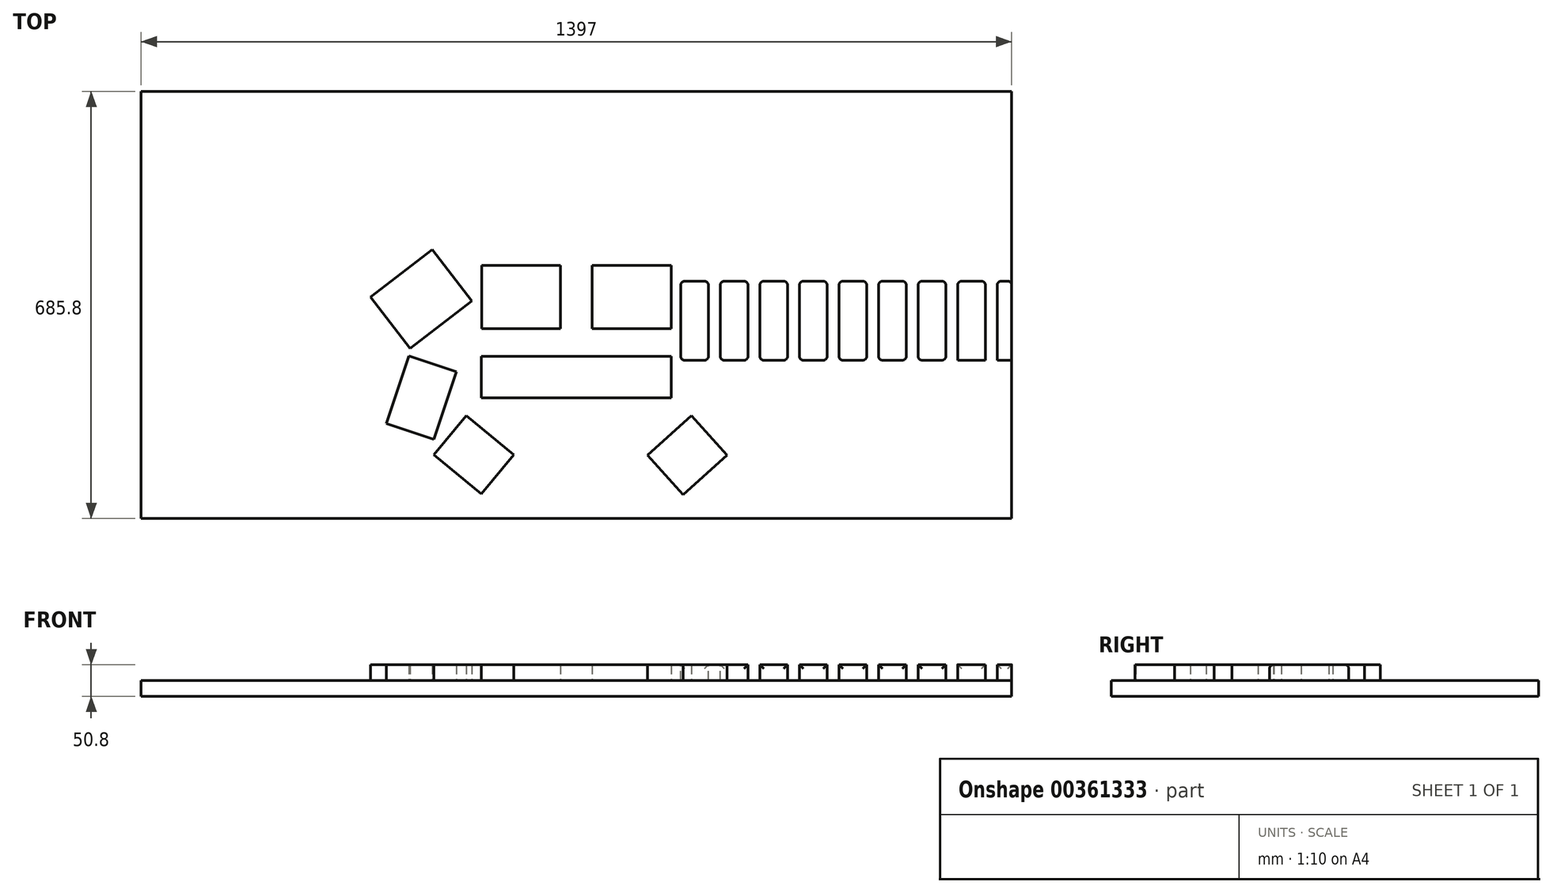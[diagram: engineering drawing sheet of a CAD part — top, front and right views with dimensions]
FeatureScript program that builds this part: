
annotation { "Feature Type Name" : "Feature", "Feature Type Description" : "" }
export const myFeature = defineFeature(function(context is Context, id is Id, definition is map)
    precondition{}
    {
        {
            var Q0;
            Q0=qCreatedBy(makeId("Top.planeOp"),FACE);
            var sketch = newSketch(context, id + "F0", { "sketchPlane" : qUnion([Q0])});
            skLineSegment(sketch, "E0.bottom", {"start": v(698.5, 313.84) * mm, "end": v(-698.5, 313.84) * mm});
            skLineSegment(sketch, "E0.top", {"start": v(698.5, -371.96) * mm, "end": v(-698.5, -371.96) * mm});
            skLineSegment(sketch, "E0.left", {"start": v(698.5, 313.84) * mm, "end": v(698.5, -371.96) * mm});
            skLineSegment(sketch, "E0.right", {"start": v(-698.5, 313.84) * mm, "end": v(-698.5, -371.96) * mm});
            skPoint(sketch, "E0.middle", {"position": v(0, -29.06) * mm});
            skSolve(sketch);
        }
        {
            var Q0;
            Q0=qSketchRegion(id+"F0",true);
            extrude(context, id + "F1", {"entities" : qUnion([Q0]), "depth" : 25.4 * mm});
        }
        {
            var Q0;
            Q0=makeQuery(id+"F1.opExtrude","CAP_FACE",FACE,{"disambiguationData":[OSD([sQuery(id+"F0.wireOp",EDGE,"E0.bottom"),sQuery(id+"F0.wireOp",EDGE,"E0.top"),sQuery(id+"F0.wireOp",EDGE,"E0.left"),sQuery(id+"F0.wireOp",EDGE,"E0.right")])],"isStart":false});
            var sketch = newSketch(context, id + "F2", { "sketchPlane" : qUnion([Q0])});
            skLineSegment(sketch, "E1.bottom", {"start": v(152.4, -111.6) * mm, "end": v(-152.4, -111.6) * mm});
            skLineSegment(sketch, "E1.top", {"start": v(152.4, -178.28) * mm, "end": v(-152.4, -178.28) * mm});
            skLineSegment(sketch, "E1.left", {"start": v(152.4, -111.6) * mm, "end": v(152.4, -178.28) * mm});
            skLineSegment(sketch, "E1.right", {"start": v(-152.4, -111.6) * mm, "end": v(-152.4, -178.28) * mm});
            skPoint(sketch, "E1.middle", {"position": v(0, -144.94) * mm});
            skLineSegment(sketch, "E2.bottom", {"start": v(-25.4, -67.16) * mm, "end": v(-151.9, -67.16) * mm});
            skLineSegment(sketch, "E2.top", {"start": v(-25.4, 34.44) * mm, "end": v(-151.9, 34.44) * mm});
            skLineSegment(sketch, "E2.left", {"start": v(-25.4, -67.16) * mm, "end": v(-25.4, 34.44) * mm});
            skLineSegment(sketch, "E2.right", {"start": v(-151.9, -67.16) * mm, "end": v(-151.9, 34.44) * mm});
            skPoint(sketch, "E2.middle", {"position": v(-88.65, -16.36) * mm});
            skPoint(sketch, "E3", {"position": v(-88.65, -67.16) * mm});
            skLineSegment(sketch, "E4.bottom", {"start": v(152.4, -67.25) * mm, "end": v(25.4, -67.25) * mm});
            skLineSegment(sketch, "E4.top", {"start": v(152.4, 34.44) * mm, "end": v(25.4, 34.44) * mm});
            skLineSegment(sketch, "E4.left", {"start": v(152.4, -67.25) * mm, "end": v(152.4, 34.44) * mm});
            skLineSegment(sketch, "E4.right", {"start": v(25.4, -67.25) * mm, "end": v(25.4, 34.44) * mm});
            skPoint(sketch, "E4.middle", {"position": v(88.9, -16.4) * mm});
            skPoint(sketch, "E5", {"position": v(88.9, -67.25) * mm});
            skLineSegment(sketch, "E6.bottom", {"start": v(-100.46, -269.65) * mm, "end": v(-152.4, -332.56) * mm});
            skLineSegment(sketch, "E6.top", {"start": v(-176.66, -206.74) * mm, "end": v(-228.6, -269.65) * mm});
            skLineSegment(sketch, "E6.left", {"start": v(-100.46, -269.65) * mm, "end": v(-176.66, -206.74) * mm});
            skLineSegment(sketch, "E6.right", {"start": v(-152.4, -332.56) * mm, "end": v(-228.6, -269.65) * mm});
            skPoint(sketch, "E6.middle", {"position": v(-164.53, -269.65) * mm});
            skLineSegment(sketch, "E7.bottom", {"start": v(-192.38, -136.29) * mm, "end": v(-228.6, -244.96) * mm});
            skLineSegment(sketch, "E7.top", {"start": v(-268.58, -110.89) * mm, "end": v(-304.8, -219.56) * mm});
            skLineSegment(sketch, "E7.left", {"start": v(-192.38, -136.29) * mm, "end": v(-268.58, -110.89) * mm});
            skLineSegment(sketch, "E7.right", {"start": v(-228.6, -244.96) * mm, "end": v(-304.8, -219.56) * mm});
            skPoint(sketch, "E7.middle", {"position": v(-248.59, -177.92) * mm});
            skLineSegment(sketch, "E8.bottom", {"start": v(-167.77, -22.8) * mm, "end": v(-266.7, -98.9) * mm});
            skLineSegment(sketch, "E8.top", {"start": v(-231.27, 59.74) * mm, "end": v(-330.2, -16.36) * mm});
            skLineSegment(sketch, "E8.left", {"start": v(-167.77, -22.8) * mm, "end": v(-231.27, 59.74) * mm});
            skLineSegment(sketch, "E8.right", {"start": v(-266.7, -98.9) * mm, "end": v(-330.2, -16.36) * mm});
            skPoint(sketch, "E8.middle", {"position": v(-248.99, -19.58) * mm});
            skLineSegment(sketch, "E9.bottom", {"start": v(114.3, -270.36) * mm, "end": v(184.86, -206.86) * mm});
            skLineSegment(sketch, "E9.top", {"start": v(171.45, -333.86) * mm, "end": v(242, -270.36) * mm});
            skLineSegment(sketch, "E9.left", {"start": v(114.3, -270.36) * mm, "end": v(171.45, -333.86) * mm});
            skLineSegment(sketch, "E9.right", {"start": v(184.86, -206.86) * mm, "end": v(242, -270.36) * mm});
            skPoint(sketch, "E9.middle", {"position": v(178.15, -270.36) * mm});
            skPoint(sketch, "E10", {"position": v(206.73, -302.1) * mm});
            skSolve(sketch);
        }
        {
            var Q0;
            Q0=qSketchRegion(id+"F2",true);
            extrude(context, id + "F3", {"entities" : qUnion([Q0]), "depth" : 25.4 * mm});
        }
        {
            var Q0;
            Q0=makeQuery(id+"F1.opExtrude","CAP_FACE",FACE,{"disambiguationData":[OSD([sQuery(id+"F0.wireOp",EDGE,"E0.bottom"),sQuery(id+"F0.wireOp",EDGE,"E0.top"),sQuery(id+"F0.wireOp",EDGE,"E0.left"),sQuery(id+"F0.wireOp",EDGE,"E0.right")])],"isStart":false});
            var sketch = newSketch(context, id + "F4", { "sketchPlane" : qUnion([Q0])});
            skLineSegment(sketch, "E11.bottom", {"start": v(802.42, -117.9) * mm, "end": v(167.42, -118.01) * mm});
            skLineSegment(sketch, "E11.top", {"start": v(802.4, 9.1) * mm, "end": v(167.4, 8.99) * mm});
            skLineSegment(sketch, "E11.left", {"start": v(802.42, -117.9) * mm, "end": v(802.4, 9.1) * mm});
            skLineSegment(sketch, "E11.right", {"start": v(167.42, -118.01) * mm, "end": v(167.4, 8.99) * mm});
            skSolve(sketch);
        }
        {
            var Q0;
            Q0 = qSketchRegion(id + "F4", true);
            extrude(context, id + "F5", {"entities" : qUnion([Q0]), "operationType" : NewBodyOperationType.ADD, "depth" : 25.4 * mm});
        }
        {
            var Q0;
            Q0=makeQuery(id+"F5.opExtrude","SWEPT_FACE",FACE,{"disambiguationData":[OSD([sQuery(id+"F4.wireOp",EDGE,"E11.bottom")])]});
            var sketch = newSketch(context, id + "F6", { "sketchPlane" : qUnion([Q0])});
            skLineSegment(sketch, "E12.bottom", {"start": v(698.48, 25.4) * mm, "end": v(802.4, 25.4) * mm});
            skLineSegment(sketch, "E12.top", {"start": v(698.48, 50.8) * mm, "end": v(802.4, 50.8) * mm});
            skLineSegment(sketch, "E12.left", {"start": v(698.48, 25.4) * mm, "end": v(698.48, 50.8) * mm});
            skLineSegment(sketch, "E12.right", {"start": v(802.4, 25.4) * mm, "end": v(802.4, 50.8) * mm});
            skPoint(sketch, "E13", {"position": v(167.4, 50.8) * mm});
            skPoint(sketch, "E14", {"position": v(211.86, 50.8) * mm});
            skPoint(sketch, "E15", {"position": v(230.9, 50.8) * mm});
            skPoint(sketch, "E16", {"position": v(275.36, 50.8) * mm});
            skPoint(sketch, "E17", {"position": v(294.4, 50.8) * mm});
            skPoint(sketch, "E18", {"position": v(338.86, 50.8) * mm});
            skPoint(sketch, "E19", {"position": v(357.9, 50.8) * mm});
            skPoint(sketch, "E20", {"position": v(402.36, 50.8) * mm});
            skPoint(sketch, "E21", {"position": v(421.4, 50.8) * mm});
            skPoint(sketch, "E22", {"position": v(465.86, 50.8) * mm});
            skPoint(sketch, "E23", {"position": v(484.9, 50.8) * mm});
            skPoint(sketch, "E24", {"position": v(529.36, 50.8) * mm});
            skPoint(sketch, "E25", {"position": v(548.4, 50.8) * mm});
            skPoint(sketch, "E26", {"position": v(592.86, 50.8) * mm});
            skPoint(sketch, "E27", {"position": v(611.9, 50.8) * mm});
            skPoint(sketch, "E28", {"position": v(656.36, 50.8) * mm});
            skPoint(sketch, "E29", {"position": v(675.4, 50.8) * mm});
            skLineSegment(sketch, "E30.bottom", {"start": v(675.4, 50.8) * mm, "end": v(656.36, 50.8) * mm});
            skLineSegment(sketch, "E30.top", {"start": v(675.4, 25.4) * mm, "end": v(656.36, 25.4) * mm});
            skLineSegment(sketch, "E30.left", {"start": v(675.4, 50.8) * mm, "end": v(675.4, 25.4) * mm});
            skLineSegment(sketch, "E30.right", {"start": v(656.36, 50.8) * mm, "end": v(656.36, 25.4) * mm});
            skLineSegment(sketch, "E31.bottom", {"start": v(611.9, 25.4) * mm, "end": v(592.86, 25.4) * mm});
            skLineSegment(sketch, "E31.top", {"start": v(611.9, 50.8) * mm, "end": v(592.86, 50.8) * mm});
            skLineSegment(sketch, "E31.left", {"start": v(611.9, 25.4) * mm, "end": v(611.9, 50.8) * mm});
            skLineSegment(sketch, "E31.right", {"start": v(592.86, 25.4) * mm, "end": v(592.86, 50.8) * mm});
            skLineSegment(sketch, "E32.bottom", {"start": v(548.4, 25.4) * mm, "end": v(529.36, 25.4) * mm});
            skLineSegment(sketch, "E32.top", {"start": v(548.4, 50.8) * mm, "end": v(529.36, 50.8) * mm});
            skLineSegment(sketch, "E32.left", {"start": v(548.4, 25.4) * mm, "end": v(548.4, 50.8) * mm});
            skLineSegment(sketch, "E32.right", {"start": v(529.36, 25.4) * mm, "end": v(529.36, 50.8) * mm});
            skLineSegment(sketch, "E33.bottom", {"start": v(484.9, 25.4) * mm, "end": v(465.86, 25.4) * mm});
            skLineSegment(sketch, "E33.top", {"start": v(484.9, 50.8) * mm, "end": v(465.86, 50.8) * mm});
            skLineSegment(sketch, "E33.left", {"start": v(484.9, 25.4) * mm, "end": v(484.9, 50.8) * mm});
            skLineSegment(sketch, "E33.right", {"start": v(465.86, 25.4) * mm, "end": v(465.86, 50.8) * mm});
            skLineSegment(sketch, "E34.bottom", {"start": v(421.4, 25.4) * mm, "end": v(402.36, 25.4) * mm});
            skLineSegment(sketch, "E34.top", {"start": v(421.4, 50.8) * mm, "end": v(402.36, 50.8) * mm});
            skLineSegment(sketch, "E34.left", {"start": v(421.4, 25.4) * mm, "end": v(421.4, 50.8) * mm});
            skLineSegment(sketch, "E34.right", {"start": v(402.36, 25.4) * mm, "end": v(402.36, 50.8) * mm});
            skLineSegment(sketch, "E35.bottom", {"start": v(357.9, 25.4) * mm, "end": v(338.86, 25.4) * mm});
            skLineSegment(sketch, "E35.top", {"start": v(357.9, 50.8) * mm, "end": v(338.86, 50.8) * mm});
            skLineSegment(sketch, "E35.left", {"start": v(357.9, 25.4) * mm, "end": v(357.9, 50.8) * mm});
            skLineSegment(sketch, "E35.right", {"start": v(338.86, 25.4) * mm, "end": v(338.86, 50.8) * mm});
            skLineSegment(sketch, "E36.bottom", {"start": v(294.4, 25.4) * mm, "end": v(275.36, 25.4) * mm});
            skLineSegment(sketch, "E36.top", {"start": v(294.4, 50.8) * mm, "end": v(275.36, 50.8) * mm});
            skLineSegment(sketch, "E36.left", {"start": v(294.4, 25.4) * mm, "end": v(294.4, 50.8) * mm});
            skLineSegment(sketch, "E36.right", {"start": v(275.36, 25.4) * mm, "end": v(275.36, 50.8) * mm});
            skLineSegment(sketch, "E37.bottom", {"start": v(230.9, 25.4) * mm, "end": v(211.86, 25.4) * mm});
            skLineSegment(sketch, "E37.top", {"start": v(230.9, 50.8) * mm, "end": v(211.86, 50.8) * mm});
            skLineSegment(sketch, "E37.left", {"start": v(230.9, 25.4) * mm, "end": v(230.9, 50.8) * mm});
            skLineSegment(sketch, "E37.right", {"start": v(211.86, 25.4) * mm, "end": v(211.86, 50.8) * mm});
            skSolve(sketch);
        }
        {
            var Q0;
            Q0 = qSketchRegion(id + "F6", true);
            extrude(context, id + "F7", {"entities" : qUnion([Q0]), "operationType" : NewBodyOperationType.REMOVE, "oppositeDirection" : true, "depth" : 203.2 * mm});
        }
        {
            var Q0;
            {var subQ0=sQuery(id+"F4.wireOp",EDGE,"E11.bottom");var subQ1=sQuery(id+"F4.wireOp",EDGE,"E11.right");Q0=makeQuery(id+"F7.boolean.opBoolean","SPLIT",EDGE,{"disambiguationData":[TD([makeQuery(id+"F5.opExtrude","SWEPT_FACE",FACE,{"disambiguationData":[OSD([subQ1])]})])],"derivedFrom":makeQuery(id+"F5.opExtrude","CAP_EDGE",EDGE,{"disambiguationData":[OSD([subQ0])],"isStart":false})});}
            var Q1;
            {var subQ0=sQuery(id+"F4.wireOp",EDGE,"E11.bottom");Q1=makeQuery(id+"F7.boolean.opBoolean","SPLIT",EDGE,{"disambiguationData":[TD([makeQuery(id+"F7.opExtrude","SWEPT_FACE",FACE,{"disambiguationData":[OSD([sQuery(id+"F6.wireOp",EDGE,"E36.right")])]})])],"derivedFrom":makeQuery(id+"F5.opExtrude","CAP_EDGE",EDGE,{"disambiguationData":[OSD([subQ0])],"isStart":false})});}
            var Q2;
            {var subQ0=sQuery(id+"F4.wireOp",EDGE,"E11.bottom");Q2=makeQuery(id+"F7.boolean.opBoolean","SPLIT",EDGE,{"disambiguationData":[TD([makeQuery(id+"F7.opExtrude","SWEPT_FACE",FACE,{"disambiguationData":[OSD([sQuery(id+"F6.wireOp",EDGE,"E35.right")])]})])],"derivedFrom":makeQuery(id+"F5.opExtrude","CAP_EDGE",EDGE,{"disambiguationData":[OSD([subQ0])],"isStart":false})});}
            var Q3;
            {var subQ0=sQuery(id+"F4.wireOp",EDGE,"E11.bottom");Q3=makeQuery(id+"F7.boolean.opBoolean","SPLIT",EDGE,{"disambiguationData":[TD([makeQuery(id+"F7.opExtrude","SWEPT_FACE",FACE,{"disambiguationData":[OSD([sQuery(id+"F6.wireOp",EDGE,"E34.right")])]})])],"derivedFrom":makeQuery(id+"F5.opExtrude","CAP_EDGE",EDGE,{"disambiguationData":[OSD([subQ0])],"isStart":false})});}
            var Q4;
            {var subQ0=sQuery(id+"F4.wireOp",EDGE,"E11.bottom");Q4=makeQuery(id+"F7.boolean.opBoolean","SPLIT",EDGE,{"disambiguationData":[TD([makeQuery(id+"F7.opExtrude","SWEPT_FACE",FACE,{"disambiguationData":[OSD([sQuery(id+"F6.wireOp",EDGE,"E33.right")])]})])],"derivedFrom":makeQuery(id+"F5.opExtrude","CAP_EDGE",EDGE,{"disambiguationData":[OSD([subQ0])],"isStart":false})});}
            var Q5;
            {var subQ0=sQuery(id+"F4.wireOp",EDGE,"E11.bottom");Q5=makeQuery(id+"F7.boolean.opBoolean","SPLIT",EDGE,{"disambiguationData":[TD([makeQuery(id+"F7.opExtrude","SWEPT_FACE",FACE,{"disambiguationData":[OSD([sQuery(id+"F6.wireOp",EDGE,"E32.right")])]})])],"derivedFrom":makeQuery(id+"F5.opExtrude","CAP_EDGE",EDGE,{"disambiguationData":[OSD([subQ0])],"isStart":false})});}
            var Q6;
            {var subQ0=sQuery(id+"F4.wireOp",EDGE,"E11.bottom");Q6=makeQuery(id+"F7.boolean.opBoolean","SPLIT",EDGE,{"disambiguationData":[TD([makeQuery(id+"F7.opExtrude","SWEPT_FACE",FACE,{"disambiguationData":[OSD([sQuery(id+"F6.wireOp",EDGE,"E31.right")])]})])],"derivedFrom":makeQuery(id+"F5.opExtrude","CAP_EDGE",EDGE,{"disambiguationData":[OSD([subQ0])],"isStart":false})});}
            var Q7;
            {var subQ0=sQuery(id+"F4.wireOp",EDGE,"E11.bottom");Q7=makeQuery(id+"F7.boolean.opBoolean","SPLIT",EDGE,{"disambiguationData":[TD([makeQuery(id+"F7.opExtrude","SWEPT_FACE",FACE,{"disambiguationData":[OSD([sQuery(id+"F6.wireOp",EDGE,"E30.right")])]})])],"derivedFrom":makeQuery(id+"F5.opExtrude","CAP_EDGE",EDGE,{"disambiguationData":[OSD([subQ0])],"isStart":false})});}
            var Q8;
            {var subQ0=sQuery(id+"F4.wireOp",EDGE,"E11.top");Q8=makeQuery(id+"F7.boolean.opBoolean","SPLIT",EDGE,{"disambiguationData":[TD([makeQuery(id+"F7.opExtrude","SWEPT_FACE",FACE,{"disambiguationData":[OSD([sQuery(id+"F6.wireOp",EDGE,"E30.right")])]})])],"derivedFrom":makeQuery(id+"F5.opExtrude","CAP_EDGE",EDGE,{"disambiguationData":[OSD([subQ0])],"isStart":false})});}
            var Q9;
            {var subQ0=sQuery(id+"F4.wireOp",EDGE,"E11.top");Q9=makeQuery(id+"F7.boolean.opBoolean","SPLIT",EDGE,{"disambiguationData":[TD([makeQuery(id+"F7.opExtrude","SWEPT_FACE",FACE,{"disambiguationData":[OSD([sQuery(id+"F6.wireOp",EDGE,"E12.left")])]})])],"derivedFrom":makeQuery(id+"F5.opExtrude","CAP_EDGE",EDGE,{"disambiguationData":[OSD([subQ0])],"isStart":false})});}
            var Q10;
            {var subQ0=sQuery(id+"F4.wireOp",EDGE,"E11.bottom");Q10=makeQuery(id+"F7.boolean.opBoolean","SPLIT",EDGE,{"disambiguationData":[TD([makeQuery(id+"F7.opExtrude","SWEPT_FACE",FACE,{"disambiguationData":[OSD([sQuery(id+"F6.wireOp",EDGE,"E12.left")])]})])],"derivedFrom":makeQuery(id+"F5.opExtrude","CAP_EDGE",EDGE,{"disambiguationData":[OSD([subQ0])],"isStart":false})});}
            var Q11;
            {var subQ0=sQuery(id+"F4.wireOp",EDGE,"E11.top");Q11=makeQuery(id+"F7.boolean.opBoolean","SPLIT",EDGE,{"disambiguationData":[TD([makeQuery(id+"F7.opExtrude","SWEPT_FACE",FACE,{"disambiguationData":[OSD([sQuery(id+"F6.wireOp",EDGE,"E31.right")])]})])],"derivedFrom":makeQuery(id+"F5.opExtrude","CAP_EDGE",EDGE,{"disambiguationData":[OSD([subQ0])],"isStart":false})});}
            var Q12;
            {var subQ0=sQuery(id+"F4.wireOp",EDGE,"E11.top");Q12=makeQuery(id+"F7.boolean.opBoolean","SPLIT",EDGE,{"disambiguationData":[TD([makeQuery(id+"F7.opExtrude","SWEPT_FACE",FACE,{"disambiguationData":[OSD([sQuery(id+"F6.wireOp",EDGE,"E32.right")])]})])],"derivedFrom":makeQuery(id+"F5.opExtrude","CAP_EDGE",EDGE,{"disambiguationData":[OSD([subQ0])],"isStart":false})});}
            var Q13;
            {var subQ0=sQuery(id+"F4.wireOp",EDGE,"E11.top");Q13=makeQuery(id+"F7.boolean.opBoolean","SPLIT",EDGE,{"disambiguationData":[TD([makeQuery(id+"F7.opExtrude","SWEPT_FACE",FACE,{"disambiguationData":[OSD([sQuery(id+"F6.wireOp",EDGE,"E33.right")])]})])],"derivedFrom":makeQuery(id+"F5.opExtrude","CAP_EDGE",EDGE,{"disambiguationData":[OSD([subQ0])],"isStart":false})});}
            var Q14;
            {var subQ0=sQuery(id+"F4.wireOp",EDGE,"E11.right");var subQ1=sQuery(id+"F4.wireOp",EDGE,"E11.top");Q14=makeQuery(id+"F7.boolean.opBoolean","SPLIT",EDGE,{"disambiguationData":[TD([makeQuery(id+"F5.opExtrude","SWEPT_FACE",FACE,{"disambiguationData":[OSD([subQ0])]})])],"derivedFrom":makeQuery(id+"F5.opExtrude","CAP_EDGE",EDGE,{"disambiguationData":[OSD([subQ1])],"isStart":false})});}
            var Q15;
            {var subQ0=sQuery(id+"F4.wireOp",EDGE,"E11.top");Q15=makeQuery(id+"F7.boolean.opBoolean","SPLIT",EDGE,{"disambiguationData":[TD([makeQuery(id+"F7.opExtrude","SWEPT_FACE",FACE,{"disambiguationData":[OSD([sQuery(id+"F6.wireOp",EDGE,"E36.right")])]})])],"derivedFrom":makeQuery(id+"F5.opExtrude","CAP_EDGE",EDGE,{"disambiguationData":[OSD([subQ0])],"isStart":false})});}
            var Q16;
            {var subQ0=sQuery(id+"F4.wireOp",EDGE,"E11.top");Q16=makeQuery(id+"F7.boolean.opBoolean","SPLIT",EDGE,{"disambiguationData":[TD([makeQuery(id+"F7.opExtrude","SWEPT_FACE",FACE,{"disambiguationData":[OSD([sQuery(id+"F6.wireOp",EDGE,"E35.right")])]})])],"derivedFrom":makeQuery(id+"F5.opExtrude","CAP_EDGE",EDGE,{"disambiguationData":[OSD([subQ0])],"isStart":false})});}
            var Q17;
            {var subQ0=sQuery(id+"F4.wireOp",EDGE,"E11.top");Q17=makeQuery(id+"F7.boolean.opBoolean","SPLIT",EDGE,{"disambiguationData":[TD([makeQuery(id+"F7.opExtrude","SWEPT_FACE",FACE,{"disambiguationData":[OSD([sQuery(id+"F6.wireOp",EDGE,"E34.right")])]})])],"derivedFrom":makeQuery(id+"F5.opExtrude","CAP_EDGE",EDGE,{"disambiguationData":[OSD([subQ0])],"isStart":false})});}
            var Q18;
            Q18=makeQuery(id+"F5.opExtrude","SWEPT_EDGE",EDGE,{"disambiguationData":[OSD([sQuery(id+"F4.wireOp",EDGE,"E11.bottom"),sQuery(id+"F4.wireOp",EDGE,"E11.right")])]});
            var Q19;
            Q19=makeQuery(id+"F7.boolean.opBoolean","COPY",EDGE,{"derivedFrom":makeQuery(id+"F7.opExtrude","CAP_EDGE",EDGE,{"disambiguationData":[OSD([sQuery(id+"F6.wireOp",EDGE,"E37.right")])],"isStart":true})});
            var Q20;
            Q20=makeQuery(id+"F7.boolean.opBoolean","COPY",EDGE,{"derivedFrom":makeQuery(id+"F7.opExtrude","CAP_EDGE",EDGE,{"disambiguationData":[OSD([sQuery(id+"F6.wireOp",EDGE,"E37.left")])],"isStart":true})});
            var Q21;
            Q21=makeQuery(id+"F7.boolean.opBoolean","COPY",EDGE,{"derivedFrom":makeQuery(id+"F7.opExtrude","CAP_EDGE",EDGE,{"disambiguationData":[OSD([sQuery(id+"F6.wireOp",EDGE,"E36.right")])],"isStart":true})});
            var Q22;
            Q22=makeQuery(id+"F7.boolean.opBoolean","COPY",EDGE,{"derivedFrom":makeQuery(id+"F7.opExtrude","CAP_EDGE",EDGE,{"disambiguationData":[OSD([sQuery(id+"F6.wireOp",EDGE,"E36.left")])],"isStart":true})});
            var Q23;
            Q23=makeQuery(id+"F7.boolean.opBoolean","COPY",EDGE,{"derivedFrom":makeQuery(id+"F7.opExtrude","CAP_EDGE",EDGE,{"disambiguationData":[OSD([sQuery(id+"F6.wireOp",EDGE,"E35.right")])],"isStart":true})});
            var Q24;
            Q24=makeQuery(id+"F7.boolean.opBoolean","COPY",EDGE,{"derivedFrom":makeQuery(id+"F7.opExtrude","CAP_EDGE",EDGE,{"disambiguationData":[OSD([sQuery(id+"F6.wireOp",EDGE,"E35.left")])],"isStart":true})});
            var Q25;
            Q25=makeQuery(id+"F7.boolean.opBoolean","COPY",EDGE,{"derivedFrom":makeQuery(id+"F7.opExtrude","CAP_EDGE",EDGE,{"disambiguationData":[OSD([sQuery(id+"F6.wireOp",EDGE,"E34.right")])],"isStart":true})});
            var Q26;
            Q26=makeQuery(id+"F7.boolean.opBoolean","COPY",EDGE,{"derivedFrom":makeQuery(id+"F7.opExtrude","CAP_EDGE",EDGE,{"disambiguationData":[OSD([sQuery(id+"F6.wireOp",EDGE,"E34.left")])],"isStart":true})});
            var Q27;
            Q27=makeQuery(id+"F7.boolean.opBoolean","COPY",EDGE,{"derivedFrom":makeQuery(id+"F7.opExtrude","CAP_EDGE",EDGE,{"disambiguationData":[OSD([sQuery(id+"F6.wireOp",EDGE,"E33.right")])],"isStart":true})});
            var Q28;
            Q28=makeQuery(id+"F7.boolean.opBoolean","COPY",EDGE,{"derivedFrom":makeQuery(id+"F7.opExtrude","CAP_EDGE",EDGE,{"disambiguationData":[OSD([sQuery(id+"F6.wireOp",EDGE,"E33.left")])],"isStart":true})});
            var Q29;
            Q29=makeQuery(id+"F7.boolean.opBoolean","COPY",EDGE,{"derivedFrom":makeQuery(id+"F7.opExtrude","CAP_EDGE",EDGE,{"disambiguationData":[OSD([sQuery(id+"F6.wireOp",EDGE,"E32.right")])],"isStart":true})});
            var Q30;
            Q30=makeQuery(id+"F7.boolean.opBoolean","COPY",EDGE,{"derivedFrom":makeQuery(id+"F7.opExtrude","CAP_EDGE",EDGE,{"disambiguationData":[OSD([sQuery(id+"F6.wireOp",EDGE,"E32.left")])],"isStart":true})});
            var Q31;
            Q31=makeQuery(id+"F7.boolean.opBoolean","COPY",EDGE,{"derivedFrom":makeQuery(id+"F7.opExtrude","CAP_EDGE",EDGE,{"disambiguationData":[OSD([sQuery(id+"F6.wireOp",EDGE,"E31.right")])],"isStart":true})});
            var Q32;
            Q32=makeQuery(id+"F7.boolean.opBoolean","COPY",EDGE,{"derivedFrom":makeQuery(id+"F7.opExtrude","CAP_EDGE",EDGE,{"disambiguationData":[OSD([sQuery(id+"F6.wireOp",EDGE,"E31.left")])],"isStart":true})});
            var Q33;
            Q33=makeQuery(id+"F7.boolean.opBoolean","COPY",EDGE,{"derivedFrom":makeQuery(id+"F7.opExtrude","CAP_EDGE",EDGE,{"disambiguationData":[OSD([sQuery(id+"F6.wireOp",EDGE,"E30.right")])],"isStart":true})});
            var Q34;
            Q34=makeQuery(id+"F7.boolean.opBoolean","INTERSECT",EDGE,{"derivedFrom":[makeQuery(id+"F5.opExtrude","SWEPT_FACE",FACE,{"disambiguationData":[OSD([sQuery(id+"F4.wireOp",EDGE,"E11.top")])]}),makeQuery(id+"F7.opExtrude","SWEPT_FACE",FACE,{"disambiguationData":[OSD([sQuery(id+"F6.wireOp",EDGE,"E37.right")])]})]});
            var Q35;
            Q35=makeQuery(id+"F5.opExtrude","SWEPT_EDGE",EDGE,{"disambiguationData":[OSD([sQuery(id+"F4.wireOp",EDGE,"E11.top"),sQuery(id+"F4.wireOp",EDGE,"E11.right")])]});
            var Q36;
            Q36=makeQuery(id+"F7.boolean.opBoolean","INTERSECT",EDGE,{"derivedFrom":[makeQuery(id+"F5.opExtrude","SWEPT_FACE",FACE,{"disambiguationData":[OSD([sQuery(id+"F4.wireOp",EDGE,"E11.top")])]}),makeQuery(id+"F7.opExtrude","SWEPT_FACE",FACE,{"disambiguationData":[OSD([sQuery(id+"F6.wireOp",EDGE,"E37.left")])]})]});
            var Q37;
            Q37=makeQuery(id+"F7.boolean.opBoolean","INTERSECT",EDGE,{"derivedFrom":[makeQuery(id+"F5.opExtrude","SWEPT_FACE",FACE,{"disambiguationData":[OSD([sQuery(id+"F4.wireOp",EDGE,"E11.top")])]}),makeQuery(id+"F7.opExtrude","SWEPT_FACE",FACE,{"disambiguationData":[OSD([sQuery(id+"F6.wireOp",EDGE,"E36.right")])]})]});
            var Q38;
            Q38=makeQuery(id+"F7.boolean.opBoolean","INTERSECT",EDGE,{"derivedFrom":[makeQuery(id+"F5.opExtrude","SWEPT_FACE",FACE,{"disambiguationData":[OSD([sQuery(id+"F4.wireOp",EDGE,"E11.top")])]}),makeQuery(id+"F7.opExtrude","SWEPT_FACE",FACE,{"disambiguationData":[OSD([sQuery(id+"F6.wireOp",EDGE,"E36.left")])]})]});
            var Q39;
            Q39=makeQuery(id+"F7.boolean.opBoolean","INTERSECT",EDGE,{"derivedFrom":[makeQuery(id+"F5.opExtrude","SWEPT_FACE",FACE,{"disambiguationData":[OSD([sQuery(id+"F4.wireOp",EDGE,"E11.top")])]}),makeQuery(id+"F7.opExtrude","SWEPT_FACE",FACE,{"disambiguationData":[OSD([sQuery(id+"F6.wireOp",EDGE,"E35.right")])]})]});
            var Q40;
            Q40=makeQuery(id+"F7.boolean.opBoolean","INTERSECT",EDGE,{"derivedFrom":[makeQuery(id+"F5.opExtrude","SWEPT_FACE",FACE,{"disambiguationData":[OSD([sQuery(id+"F4.wireOp",EDGE,"E11.top")])]}),makeQuery(id+"F7.opExtrude","SWEPT_FACE",FACE,{"disambiguationData":[OSD([sQuery(id+"F6.wireOp",EDGE,"E35.left")])]})]});
            var Q41;
            Q41=makeQuery(id+"F7.boolean.opBoolean","INTERSECT",EDGE,{"derivedFrom":[makeQuery(id+"F5.opExtrude","SWEPT_FACE",FACE,{"disambiguationData":[OSD([sQuery(id+"F4.wireOp",EDGE,"E11.top")])]}),makeQuery(id+"F7.opExtrude","SWEPT_FACE",FACE,{"disambiguationData":[OSD([sQuery(id+"F6.wireOp",EDGE,"E34.right")])]})]});
            var Q42;
            Q42=makeQuery(id+"F7.boolean.opBoolean","INTERSECT",EDGE,{"derivedFrom":[makeQuery(id+"F5.opExtrude","SWEPT_FACE",FACE,{"disambiguationData":[OSD([sQuery(id+"F4.wireOp",EDGE,"E11.top")])]}),makeQuery(id+"F7.opExtrude","SWEPT_FACE",FACE,{"disambiguationData":[OSD([sQuery(id+"F6.wireOp",EDGE,"E34.left")])]})]});
            var Q43;
            Q43=makeQuery(id+"F7.boolean.opBoolean","INTERSECT",EDGE,{"derivedFrom":[makeQuery(id+"F5.opExtrude","SWEPT_FACE",FACE,{"disambiguationData":[OSD([sQuery(id+"F4.wireOp",EDGE,"E11.top")])]}),makeQuery(id+"F7.opExtrude","SWEPT_FACE",FACE,{"disambiguationData":[OSD([sQuery(id+"F6.wireOp",EDGE,"E33.right")])]})]});
            var Q44;
            Q44=makeQuery(id+"F7.boolean.opBoolean","INTERSECT",EDGE,{"derivedFrom":[makeQuery(id+"F5.opExtrude","SWEPT_FACE",FACE,{"disambiguationData":[OSD([sQuery(id+"F4.wireOp",EDGE,"E11.top")])]}),makeQuery(id+"F7.opExtrude","SWEPT_FACE",FACE,{"disambiguationData":[OSD([sQuery(id+"F6.wireOp",EDGE,"E33.left")])]})]});
            var Q45;
            Q45=makeQuery(id+"F7.boolean.opBoolean","INTERSECT",EDGE,{"derivedFrom":[makeQuery(id+"F5.opExtrude","SWEPT_FACE",FACE,{"disambiguationData":[OSD([sQuery(id+"F4.wireOp",EDGE,"E11.top")])]}),makeQuery(id+"F7.opExtrude","SWEPT_FACE",FACE,{"disambiguationData":[OSD([sQuery(id+"F6.wireOp",EDGE,"E32.right")])]})]});
            var Q46;
            Q46=makeQuery(id+"F7.boolean.opBoolean","INTERSECT",EDGE,{"derivedFrom":[makeQuery(id+"F5.opExtrude","SWEPT_FACE",FACE,{"disambiguationData":[OSD([sQuery(id+"F4.wireOp",EDGE,"E11.top")])]}),makeQuery(id+"F7.opExtrude","SWEPT_FACE",FACE,{"disambiguationData":[OSD([sQuery(id+"F6.wireOp",EDGE,"E32.left")])]})]});
            var Q47;
            Q47=makeQuery(id+"F7.boolean.opBoolean","INTERSECT",EDGE,{"derivedFrom":[makeQuery(id+"F5.opExtrude","SWEPT_FACE",FACE,{"disambiguationData":[OSD([sQuery(id+"F4.wireOp",EDGE,"E11.top")])]}),makeQuery(id+"F7.opExtrude","SWEPT_FACE",FACE,{"disambiguationData":[OSD([sQuery(id+"F6.wireOp",EDGE,"E31.right")])]})]});
            var Q48;
            Q48=makeQuery(id+"F7.boolean.opBoolean","INTERSECT",EDGE,{"derivedFrom":[makeQuery(id+"F5.opExtrude","SWEPT_FACE",FACE,{"disambiguationData":[OSD([sQuery(id+"F4.wireOp",EDGE,"E11.top")])]}),makeQuery(id+"F7.opExtrude","SWEPT_FACE",FACE,{"disambiguationData":[OSD([sQuery(id+"F6.wireOp",EDGE,"E31.left")])]})]});
            var Q49;
            Q49=makeQuery(id+"F7.boolean.opBoolean","INTERSECT",EDGE,{"derivedFrom":[makeQuery(id+"F5.opExtrude","SWEPT_FACE",FACE,{"disambiguationData":[OSD([sQuery(id+"F4.wireOp",EDGE,"E11.top")])]}),makeQuery(id+"F7.opExtrude","SWEPT_FACE",FACE,{"disambiguationData":[OSD([sQuery(id+"F6.wireOp",EDGE,"E30.right")])]})]});
            var Q50;
            Q50=makeQuery(id+"F7.boolean.opBoolean","INTERSECT",EDGE,{"derivedFrom":[makeQuery(id+"F5.opExtrude","SWEPT_FACE",FACE,{"disambiguationData":[OSD([sQuery(id+"F4.wireOp",EDGE,"E11.top")])]}),makeQuery(id+"F7.opExtrude","SWEPT_FACE",FACE,{"disambiguationData":[OSD([sQuery(id+"F6.wireOp",EDGE,"E30.left")])]})]});
            var Q51;
            Q51=makeQuery(id+"F7.boolean.opBoolean","INTERSECT",EDGE,{"derivedFrom":[makeQuery(id+"F5.opExtrude","SWEPT_FACE",FACE,{"disambiguationData":[OSD([sQuery(id+"F4.wireOp",EDGE,"E11.top")])]}),makeQuery(id+"F7.opExtrude","SWEPT_FACE",FACE,{"disambiguationData":[OSD([sQuery(id+"F6.wireOp",EDGE,"E12.left")])]})]});
            fillet(context, id + "F8", {"entities" : qUnion([Q0, Q1, Q2, Q3, Q4, Q5, Q6, Q7, Q8, Q9, Q10, Q11, Q12, Q13, Q14, Q15, Q16, Q17, Q18, Q19, Q20, Q21, Q22, Q23, Q24, Q25, Q26, Q27, Q28, Q29, Q30, Q31, Q32, Q33, Q34, Q35, Q36, Q37, Q38, Q39, Q40, Q41, Q42, Q43, Q44, Q45, Q46, Q47, Q48, Q49, Q50, Q51]), "radius" : 6.35 * mm, "tangentPropagation" : true, "allowEdgeOverflow" : false});
        }
        {
            var Q0;
            Q0 = qSketchRegion(id + "F2", true);
            extrude(context, id + "F9", {"entities" : qUnion([Q0]), "depth" : 25.4 * mm});
        }
    });
